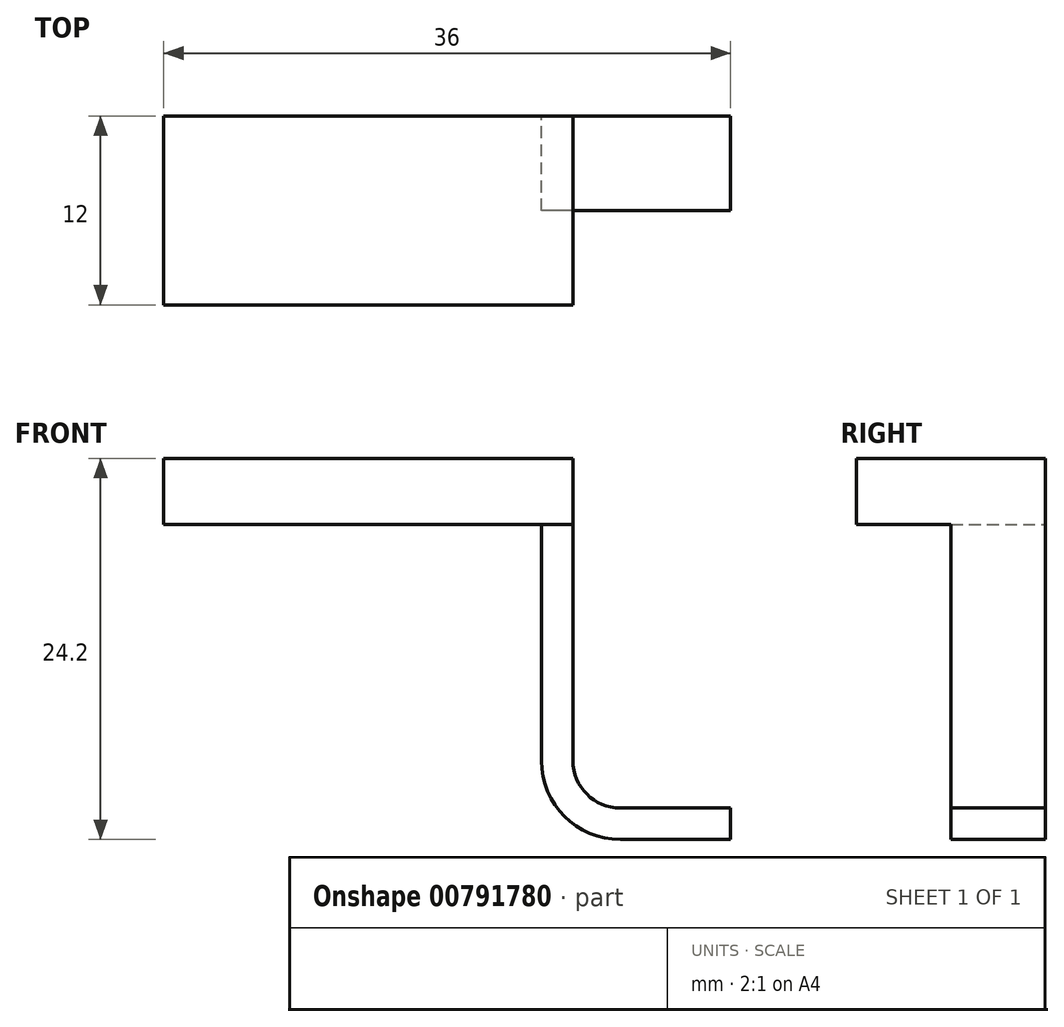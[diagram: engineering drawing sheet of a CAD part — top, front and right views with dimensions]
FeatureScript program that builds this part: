
annotation { "Feature Type Name" : "Feature", "Feature Type Description" : "" }
export const myFeature = defineFeature(function(context is Context, id is Id, definition is map)
    precondition{}
    {
        {
            var Q0;
            Q0=qCreatedBy(makeId("Front.planeOp"),FACE);
            var sketch = newSketch(context, id + "F0", { "sketchPlane" : qUnion([Q0])});
            skLineSegment(sketch, "E0", {"start": v(-24, 4.2) * mm, "end": v(2, 4.2) * mm});
            skLineSegment(sketch, "E1", {"start": v(2, 4.2) * mm, "end": v(2, -15) * mm});
            skLineSegment(sketch, "E2", {"start": v(5, -18) * mm, "end": v(12, -18) * mm});
            skLineSegment(sketch, "E3", {"start": v(12, -18) * mm, "end": v(12, -20) * mm});
            skLineSegment(sketch, "E4", {"start": v(12, -20) * mm, "end": v(5, -20) * mm});
            skLineSegment(sketch, "E5", {"start": v(0, -15) * mm, "end": v(0, 0) * mm});
            skLineSegment(sketch, "E6", {"start": v(0, 0) * mm, "end": v(-24, 0) * mm});
            skLineSegment(sketch, "E7", {"start": v(-24, 0) * mm, "end": v(-24, 4.2) * mm});
            skPoint(sketch, "E8.visualSharp", {"position": v(0, -20) * mm});
            skArc(sketch, "E8.filletArc", {"start": v(0, -15) * mm, "mid": v(1.46, -18.54) * mm, "end": v(5, -20) * mm});
            skPoint(sketch, "E9.visualSharp", {"position": v(2, -18) * mm});
            skArc(sketch, "E9.filletArc", {"start": v(2, -15) * mm, "mid": v(2.88, -17.12) * mm, "end": v(5, -18) * mm});
            skSolve(sketch);
        }
        {
            var Q0;
            Q0=makeQuery(id+"F0.imprint","IMPRINT",FACE,{"disambiguationData":[TD([[makeQuery(id+"F0.imprint","IMPRINT",EDGE,{"derivedFrom":sQuery(id+"F0.wireOp",EDGE,"E0")}),-1.0]])]});
            extrude(context, id + "F1", {"entities" : qUnion([Q0]), "depth" : 12 * mm, "offsetDistance" : 25 * mm});
        }
        {
            var Q0;
            Q0=qCreatedBy(makeId("Right.planeOp"),FACE);
            var sketch = newSketch(context, id + "F2", { "sketchPlane" : qUnion([Q0])});
            skLineSegment(sketch, "E10.bottom", {"start": v(-16.54, 0) * mm, "end": v(-6, 0) * mm});
            skLineSegment(sketch, "E10.top", {"start": v(-16.54, -23.22) * mm, "end": v(-6, -23.22) * mm});
            skLineSegment(sketch, "E10.left", {"start": v(-16.54, 0) * mm, "end": v(-16.54, -23.22) * mm});
            skLineSegment(sketch, "E10.right", {"start": v(-6, 0) * mm, "end": v(-6, -23.22) * mm});
            skSolve(sketch);
        }
        {
            var Q0;
            Q0 = qSketchRegion(id + "F2", true);
            extrude(context, id + "F3", {"entities" : qUnion([Q0]), "operationType" : NewBodyOperationType.REMOVE, "depth" : 25 * mm, "offsetDistance" : 25 * mm});
        }
    });
